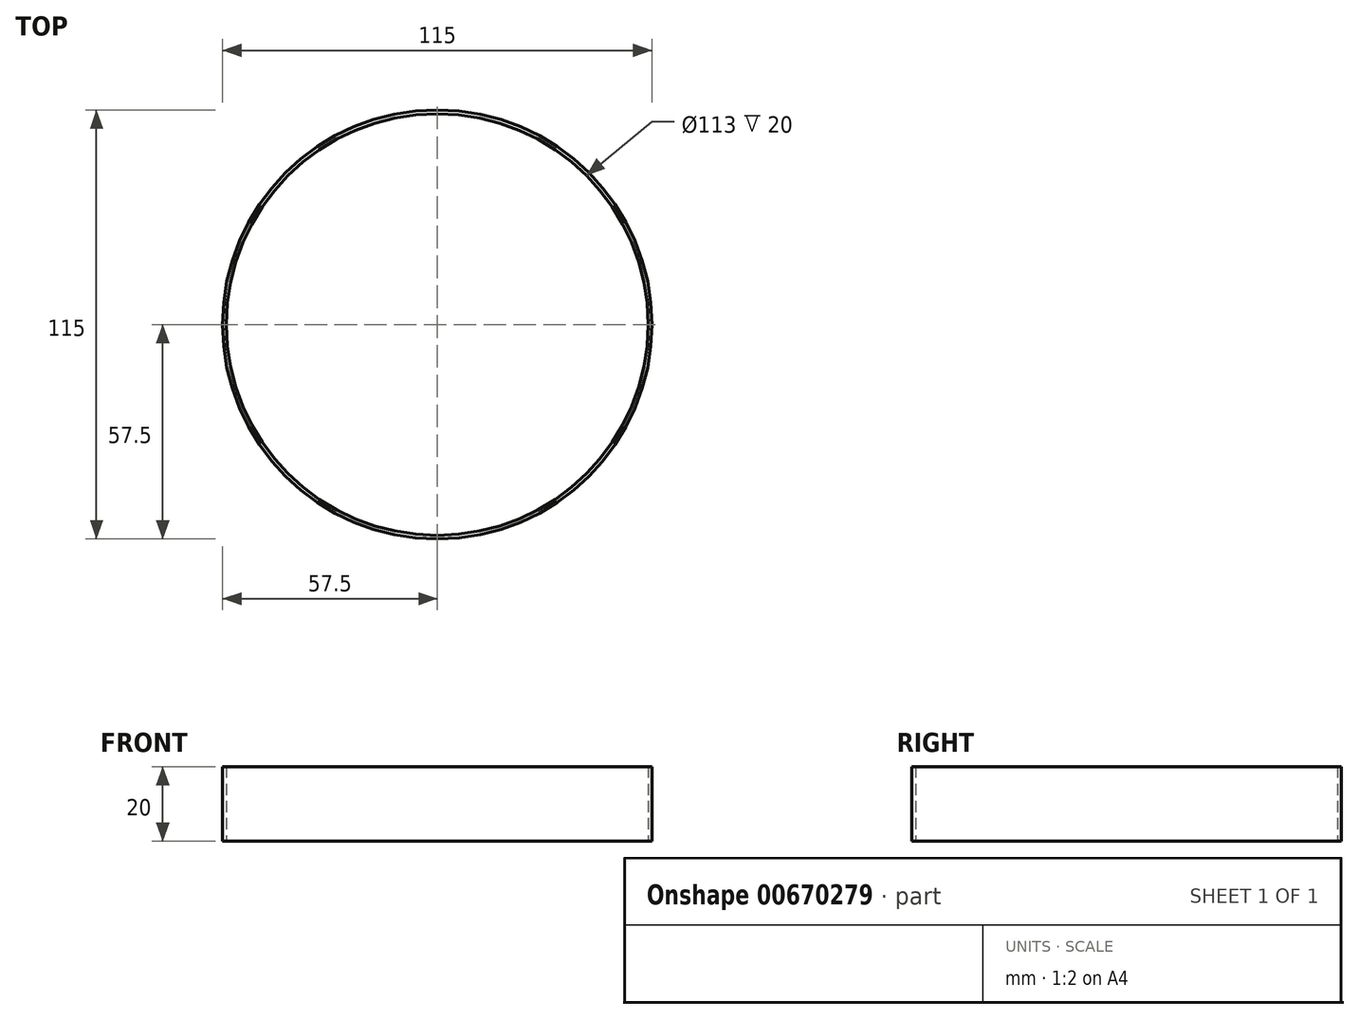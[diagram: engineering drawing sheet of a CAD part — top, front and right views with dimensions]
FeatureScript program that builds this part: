
annotation { "Feature Type Name" : "Feature", "Feature Type Description" : "" }
export const myFeature = defineFeature(function(context is Context, id is Id, definition is map)
    precondition{}
    {
        {
            var Q0;
            Q0=qCreatedBy(makeId("Top.planeOp"),FACE);
            var sketch = newSketch(context, id + "F0", { "sketchPlane" : qUnion([Q0])});
            skCircle(sketch, "E0", {"center": v(0, 0) * mm, "radius": 57.5 * mm});
            skCircle(sketch, "E1", {"center": v(0, 0) * mm, "radius": 56.5 * mm});
            skSolve(sketch);
        }
        {
            var Q0;
            Q0=makeQuery(id+"F0.imprint","IMPRINT",FACE,{"disambiguationData":[TD([[makeQuery(id+"F0.imprint","IMPRINT",EDGE,{"derivedFrom":sQuery(id+"F0.wireOp",EDGE,"E0")}),1.0]])]});
            extrude(context, id + "F1", {"entities" : qUnion([Q0]), "depth" : 20 * mm, "offsetDistance" : 25 * mm});
        }
    });
